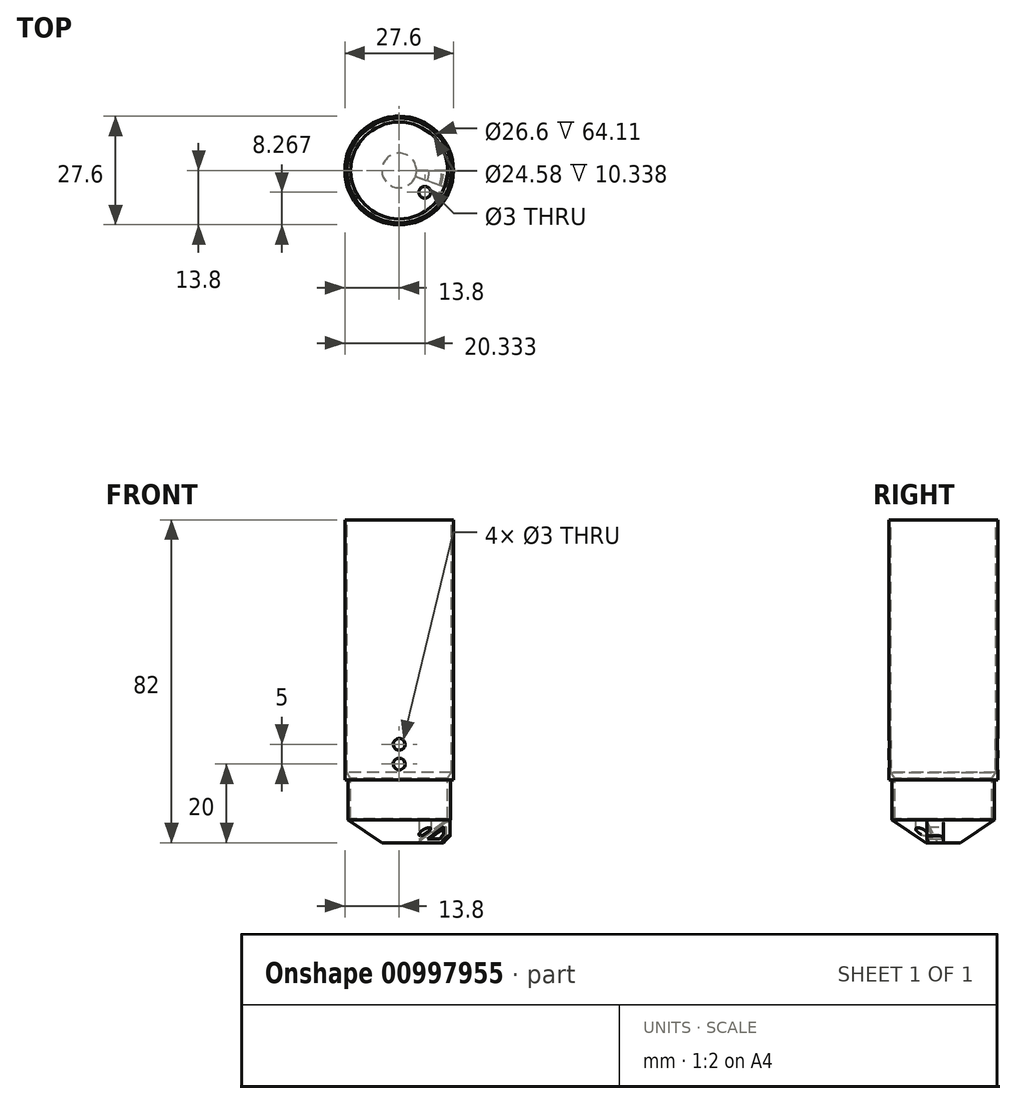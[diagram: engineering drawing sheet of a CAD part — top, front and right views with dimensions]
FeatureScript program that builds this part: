
annotation { "Feature Type Name" : "Feature", "Feature Type Description" : "" }
export const myFeature = defineFeature(function(context is Context, id is Id, definition is map)
    precondition{}
    {
        {
            var Q0;
            Q0=qCreatedBy(makeId("Front.planeOp"),FACE);
            var sketch = newSketch(context, id + "F0", { "sketchPlane" : qUnion([Q0])});
            skLineSegment(sketch, "E0", {"start": v(13, 16) * mm, "end": v(13.8, 16) * mm});
            skLineSegment(sketch, "E1", {"start": v(13.8, 16) * mm, "end": v(13.8, 82) * mm});
            skLineSegment(sketch, "E2", {"start": v(13.8, 82) * mm, "end": v(13.3, 82) * mm});
            skLineSegment(sketch, "E3", {"start": v(0, 0) * mm, "end": v(0, 1.47) * mm, "construction": true});
            skLineSegment(sketch, "E4", {"start": v(0, 0) * mm, "end": v(4.38, 0) * mm});
            skLineSegment(sketch, "E5", {"start": v(4.38, 0) * mm, "end": v(13, 5.77) * mm});
            skLineSegment(sketch, "E6", {"start": v(12.3, 16.4) * mm, "end": v(12.3, 6.05) * mm});
            skLineSegment(sketch, "E7", {"start": v(0, 6.05) * mm, "end": v(0, 0) * mm});
            skLineSegment(sketch, "E8", {"start": v(12.3, 16.4) * mm, "end": v(13.3, 17.9) * mm});
            skLineSegment(sketch, "E9", {"start": v(13.3, 82) * mm, "end": v(13.3, 17.9) * mm});
            skLineSegment(sketch, "E10", {"start": v(13, 16) * mm, "end": v(13, 5.77) * mm});
            skLineSegment(sketch, "E11", {"start": v(12.3, 6.05) * mm, "end": v(0, 6.05) * mm});
            skSolve(sketch);
        }
        {
            var Q0;
            Q0=makeQuery(id+"F0.imprint","IMPRINT",FACE,{"disambiguationData":[TD([[makeQuery(id+"F0.imprint","IMPRINT",EDGE,{"derivedFrom":sQuery(id+"F0.wireOp",EDGE,"E0")}),1.0]])]});
            var Q1;
            Q1=sQuery(id+"F0.wireOp",EDGE,"E7");
            revolve(context, id + "F1", {"surfaceOperationType" : NewSurfaceOperationType.NEW, "entities" : qUnion([Q0]), "axis" : qUnion([Q1]), "revolveType" : RevolveType.FULL});
        }
        {
            var Q0;
            Q0=qCreatedBy(makeId("Front.planeOp"),FACE);
            var sketch = newSketch(context, id + "F2", { "sketchPlane" : qUnion([Q0])});
            skCircle(sketch, "E12", {"center": v(0, 20) * mm, "radius": 1.5 * mm});
            skCircle(sketch, "E13", {"center": v(0, 25) * mm, "radius": 1.5 * mm});
            skLineSegment(sketch, "E14.0", {"start": v(13.8, 16) * mm, "end": v(-13.8, 16) * mm});
            skSolve(sketch);
        }
        {
            var Q0;
            Q0=makeQuery(id+"F2.imprint","IMPRINT",FACE,{"disambiguationData":[TD([[makeQuery(id+"F2.imprint","IMPRINT",EDGE,{"derivedFrom":sQuery(id+"F2.wireOp",EDGE,"E13")}),1.0]])]});
            var Q1;
            Q1=makeQuery(id+"F2.imprint","IMPRINT",FACE,{"disambiguationData":[TD([[makeQuery(id+"F2.imprint","IMPRINT",EDGE,{"derivedFrom":sQuery(id+"F2.wireOp",EDGE,"E12")}),1.0]])]});
            var Q2;
            Q2=sQuery(id+"F2.wireOp",EDGE,"E13");
            extrude(context, id + "F3", {"entities" : qUnion([Q0, Q1]), "operationType" : NewBodyOperationType.REMOVE, "surfaceEntities" : qUnion([Q2]), "endBound" : BoundingType.SYMMETRIC, "oppositeDirection" : true, "depth" : 40 * mm, "offsetDistance" : 25 * mm});
        }
        {
            var Q0;
            Q0=qCreatedBy(makeId("Front.planeOp"),FACE);
            var sketch = newSketch(context, id + "F4", { "sketchPlane" : qUnion([Q0])});
            skLineSegment(sketch, "E15", {"start": v(4.41, 0) * mm, "end": v(11.27, 0) * mm});
            skLineSegment(sketch, "E16", {"start": v(11.27, 0) * mm, "end": v(13, 1.75) * mm});
            skLineSegment(sketch, "E17", {"start": v(13, 1.75) * mm, "end": v(13, 5.9) * mm});
            skLineSegment(sketch, "E18", {"start": v(13, 5.9) * mm, "end": v(4.41, 0) * mm});
            skLineSegment(sketch, "E19.0", {"start": v(12, 4) * mm, "end": v(7.63, 1) * mm});
            skLineSegment(sketch, "E19.1", {"start": v(12, 2.16) * mm, "end": v(12, 4) * mm});
            skLineSegment(sketch, "E19.2", {"start": v(10.85, 1) * mm, "end": v(12, 2.16) * mm});
            skLineSegment(sketch, "E19.3", {"start": v(7.63, 1) * mm, "end": v(10.85, 1) * mm});
            skSolve(sketch);
        }
        {
            var Q0;
            Q0=makeQuery(id+"F4.imprint","IMPRINT",FACE,{"disambiguationData":[TD([[makeQuery(id+"F4.imprint","IMPRINT",EDGE,{"derivedFrom":sQuery(id+"F4.wireOp",EDGE,"E15")}),1.0]])]});
            var Q1;
            Q1=sQuery(id+"F0.wireOp",EDGE,"E7");
            revolve(context, id + "F5", {"surfaceOperationType" : NewSurfaceOperationType.NEW, "entities" : qUnion([Q0]), "axis" : qUnion([Q1]), "revolveType" : RevolveType.ONE_DIRECTION, "angle" : 20 * degree});
        }
        {
            var Q0;
            Q0=makeQuery(id+"F5.opRevolve","CAP_EDGE",EDGE,{"disambiguationData":[OSD([sQuery(id+"F4.wireOp",EDGE,"E17")])],"isStart":false});
            var Q1;
            Q1=makeQuery(id+"F5.opRevolve","CAP_EDGE",EDGE,{"disambiguationData":[OSD([sQuery(id+"F4.wireOp",EDGE,"E17")])],"isStart":true});
            fillet(context, id + "F6", {"entities" : qUnion([Q0, Q1]), "radius" : 1 * mm, "tangentPropagation" : true, "allowEdgeOverflow" : false});
        }
        {
            var Q0;
            Q0=qCreatedBy(makeId("Top.planeOp"),FACE);
            var sketch = newSketch(context, id + "F7", { "sketchPlane" : qUnion([Q0])});
            skLineSegment(sketch, "E20", {"start": v(13.07, 0) * mm, "end": v(0, 0) * mm, "construction": true});
            skLineSegment(sketch, "E21", {"start": v(6.53, 0) * mm, "end": v(6.53, -5.53) * mm, "construction": true});
            skCircle(sketch, "E22", {"center": v(6.53, -5.53) * mm, "radius": 1.5 * mm});
            skSolve(sketch);
        }
        {
            var Q0;
            Q0=makeQuery(id+"F7.imprint","IMPRINT",FACE,{"disambiguationData":[TD([[makeQuery(id+"F7.imprint","IMPRINT",EDGE,{"derivedFrom":sQuery(id+"F7.wireOp",EDGE,"E22")}),1.0]])]});
            extrude(context, id + "F8", {"entities" : qUnion([Q0]), "operationType" : NewBodyOperationType.REMOVE, "depth" : 40 * mm, "offsetDistance" : 25 * mm});
        }
    });
